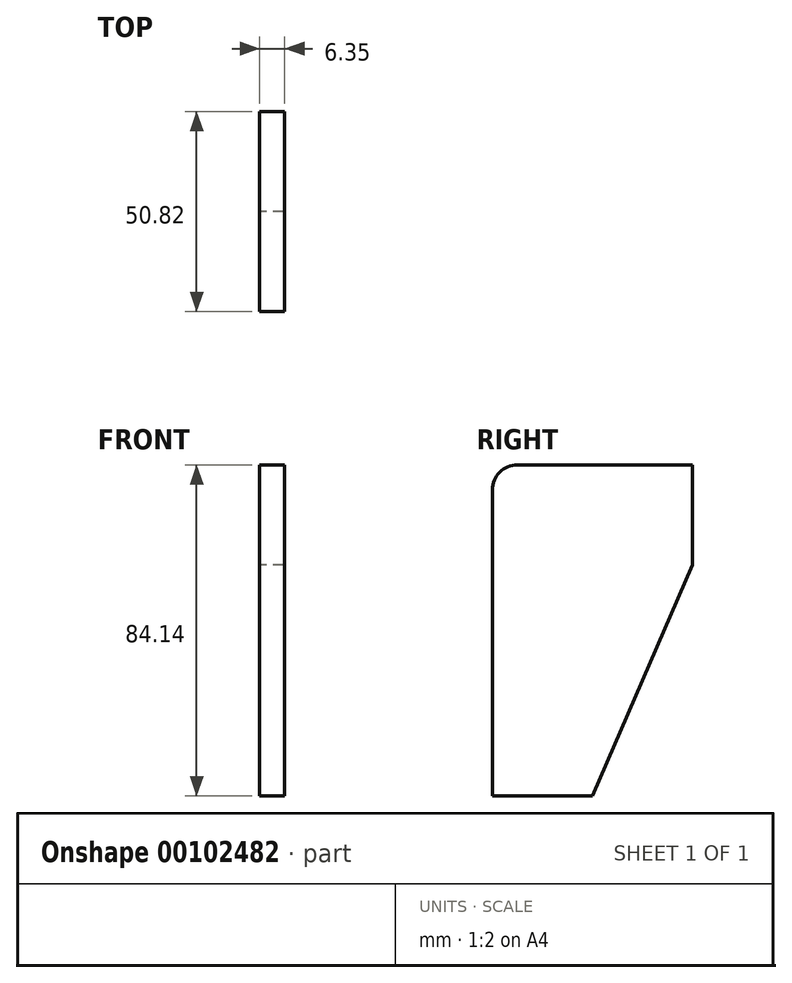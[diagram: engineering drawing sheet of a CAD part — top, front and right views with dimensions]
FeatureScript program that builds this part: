
annotation { "Feature Type Name" : "Feature", "Feature Type Description" : "" }
export const myFeature = defineFeature(function(context is Context, id is Id, definition is map)
    precondition{}
    {
        {
            var Q0;
            Q0=qCreatedBy(makeId("Right.planeOp"),FACE);
            var sketch = newSketch(context, id + "F0", { "sketchPlane" : qUnion([Q0])});
            skLineSegment(sketch, "E0", {"start": v(-25.41, -42.07) * mm, "end": v(-0.01, -42.07) * mm});
            skLineSegment(sketch, "E1", {"start": v(-0.01, -42.07) * mm, "end": v(25.39, 16.67) * mm});
            skLineSegment(sketch, "E2", {"start": v(25.39, 16.67) * mm, "end": v(25.41, 42.07) * mm});
            skLineSegment(sketch, "E3", {"start": v(25.41, 42.07) * mm, "end": v(-19.06, 42.07) * mm});
            skLineSegment(sketch, "E4", {"start": v(-25.41, -42.07) * mm, "end": v(-25.41, 35.72) * mm});
            skArc(sketch, "E5", {"start": v(-19.06, 42.07) * mm, "mid": v(-23.55, 40.2) * mm, "end": v(-25.41, 35.72) * mm});
            skSolve(sketch);
        }
        {
            var Q0;
            Q0 = qSketchRegion(id + "F0", true);
            extrude(context, id + "F1", {"entities" : qUnion([Q0]), "depth" : 6.35 * mm});
        }
    });
